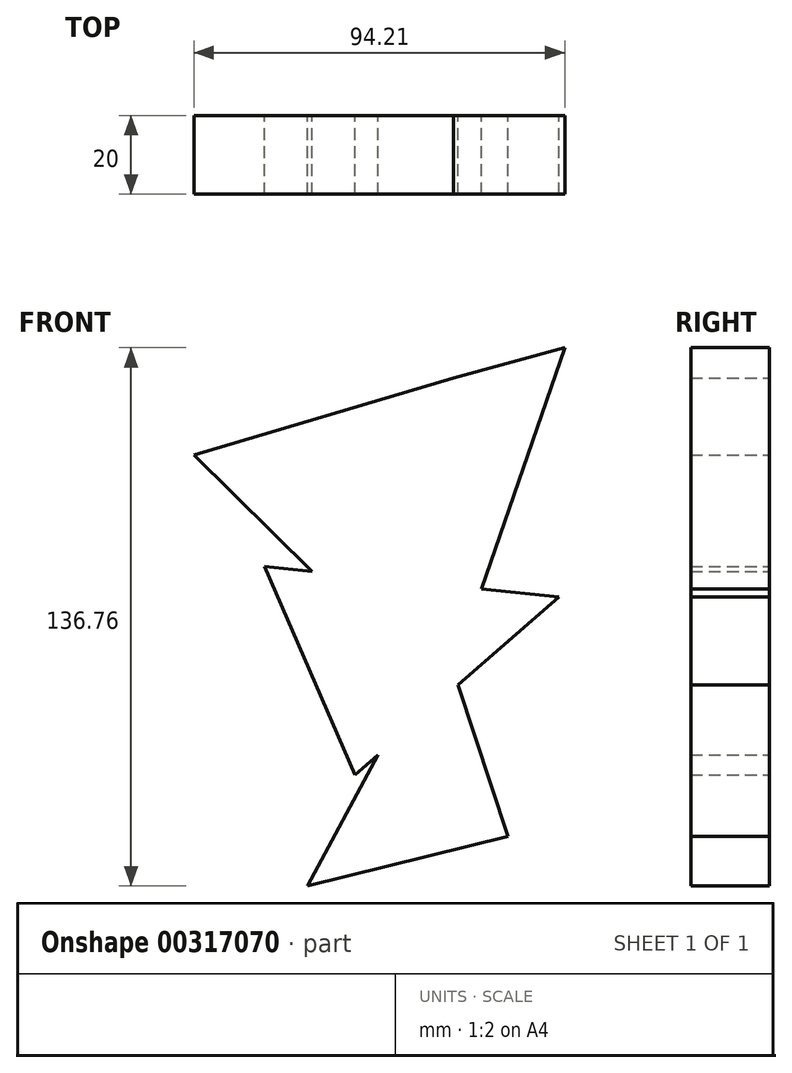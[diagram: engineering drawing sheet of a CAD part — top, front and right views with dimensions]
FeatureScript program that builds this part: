
annotation { "Feature Type Name" : "Feature", "Feature Type Description" : "" }
export const myFeature = defineFeature(function(context is Context, id is Id, definition is map)
    precondition{}
    {
        {
            var Q0;
            Q0=qCreatedBy(makeId("Front.planeOp"),FACE);
            var sketch = newSketch(context, id + "F0", { "sketchPlane" : qUnion([Q0])});
            skLineSegment(sketch, "E0", {"start": v(0, 0) * mm, "end": v(-55.6, 55) * mm});
            skLineSegment(sketch, "E1", {"start": v(-55.6, 55) * mm, "end": v(10.3, 74.53) * mm});
            skLineSegment(sketch, "E2", {"start": v(0, -4.78) * mm, "end": v(-26.77, -54.57) * mm});
            skLineSegment(sketch, "E3", {"start": v(-26.77, -54.57) * mm, "end": v(24.2, -41.92) * mm});
            skLineSegment(sketch, "E4", {"start": v(10.3, 74.53) * mm, "end": v(38.6, 82.19) * mm});
            skLineSegment(sketch, "E5", {"start": v(38.6, 82.19) * mm, "end": v(10.3, 0) * mm});
            skLineSegment(sketch, "E6", {"start": v(10.3, 0) * mm, "end": v(24.2, -41.92) * mm});
            skLineSegment(sketch, "E7", {"start": v(0, -4.78) * mm, "end": v(-16.8, 16.62) * mm});
            skLineSegment(sketch, "E8", {"start": v(37.09, 18.85) * mm, "end": v(-14.66, -26.32) * mm});
            skLineSegment(sketch, "E9", {"start": v(-14.66, -26.32) * mm, "end": v(-37.69, 26.62) * mm});
            skLineSegment(sketch, "E10", {"start": v(37.09, 18.85) * mm, "end": v(-37.69, 26.62) * mm});
            skSolve(sketch);
        }
        {
            var Q0;
            Q0 = qSketchRegion(id + "F0", true);
            extrude(context, id + "F1", {"entities" : qUnion([Q0]), "depth" : 20 * mm});
        }
    });
